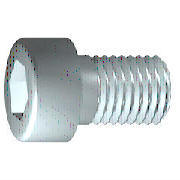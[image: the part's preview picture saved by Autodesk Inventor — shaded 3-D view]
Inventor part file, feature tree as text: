
AUTODESK INVENTOR PART (.ipt)
format: ipt  version: 2024 (Build 280153000, 153)  size: 187,392 bytes
history: native  units: mm (DEFAULTED — no unit token found)
features: extrude x1, plane x1, fillet x1
ambient origin geometry x7: Origin, YZ Plane, XY Plane, X Axis, Y Axis, Z Axis, Center Point
bodies: Solid1 (feature_tree), Body (feature_tree)
feature tree (3):
  extrude  "Slot"  Depth=22.9mm
  plane  "Work Plane1"
  fillet  "Fillet2"  Radius=0.429515mm
